# Revit family: AirTerminal_Diffuser-RoundCeiling_Bradflo_ARCD
name_source: partatom
category: Air Terminals
units: mm (PartAtom-declared; Revit-internal decimal feet)

## family parameters
Cut with Voids When Loaded = No
Host = Face
OmniClass Number = 23.75.70.21.27.11
OmniClass Title = Diffusers, Registers, and Grilles
Part Type = Normal
Room Calculation Point = No
Round Connector Dimension = Use Radius
Shared = No

## types (4) — shared parameters
Assembly Code = D3040100
Description = All Bradflo Round Diffusers can be used for supply, exhaust and return air applications. They come in both round and multiple cone types.
DiffuserMaterial = Powdercoated-White
Manufacturer = Bradflo
Model = ARCD
ModifiedIssue_ANZRS = 20140919.53 $
Type Comments = The diffuser has a round spigot to suit flexible duct. The core is adjustable and acts as both balancing damper and pattern control.Available in listed sizes
URL = www.bradflo.com.au
zero-valued in all types: Cost, Default Elevation

## per-type parameters (varying)
| type | A | B | C | ConeDiameter | DuctRadius |
| ARCD300 | 300 mm | 460 mm  [stored 1.50919 ft] | 190 mm | 340 mm | 150 mm |
| ARCD250 | 250 mm  [stored 0.82021 ft] | 410 mm  [stored 1.34514 ft] | 175 mm  [stored 0.574147 ft] | 303 mm | 125 mm  [stored 0.410105 ft] |
| ARCD200 | 200 mm  [stored 0.656168 ft] | 360 mm  [stored 1.1811 ft] | 165 mm | 266 mm | 100 mm  [stored 0.328084 ft] |
| ARCD150 | 150 mm | 310 mm  [stored 1.01706 ft] | 145 mm  [stored 0.475722 ft] | 229 mm | 75 mm |

note: column(s) folded — value = type name in every type: Type

note: [stored X ft] marks values corroborated as IEEE doubles in the binary element streams (Revit-internal decimal feet)

## geometry (parser evidence)
native form markers: Sweep x3
no freeform markers — native parametric forms only
